# Revit family: 1SE_Trez_Door_Sgl_Half_D1H
name_source: partatom
category: Specialty Equipment
units: mm (PartAtom-declared; Revit-internal decimal feet)

## family parameters
Cut with Voids When Loaded = No
Host = Face
Part Type = Normal
Room Calculation Point = No
Round Connector Dimension = Use Diameter
Shared = No

## types (2) — shared parameters
Clear Height = 1100 mm
Description = Single Door side hinged. (Half) Industrial lift door made via a new technology without welding. The locks and the hinges are outside the door for a 180-degree opening. The door complies with ЕN81-20 and EN 81-50. The door lock has a CE mark for safety regarding Lifts Directive 2014/33/EU or 2006/42/EC.
Frame Material = TREZ_Steel_Frame
Manufacturer = TREZ Ltd.
Model = D1 Half
Panel Material = TREZ_Steel_Door_Panel
Real Height = 1100 mm
Side Profiles = 50 mm  [stored 0.164042 ft]
Thickness = 45 mm  [stored 0.147638 ft]
URL = https://trez.bg
zero-valued in all types: Default Elevation

## per-type parameters (varying)
| type | Clear Width | Real Width |
| 1300x1100mm | 1300 mm  [stored 4.26509 ft] | 1300 mm  [stored 4.26509 ft] |
| 1700x1100mm | 1700 mm  [stored 5.57743 ft] | 1400 mm  [stored 4.59318 ft] |

note: [stored X ft] marks values corroborated as IEEE doubles in the binary element streams (Revit-internal decimal feet)

## geometry (parser evidence)
native form markers: Sweep x8
no freeform markers — native parametric forms only
